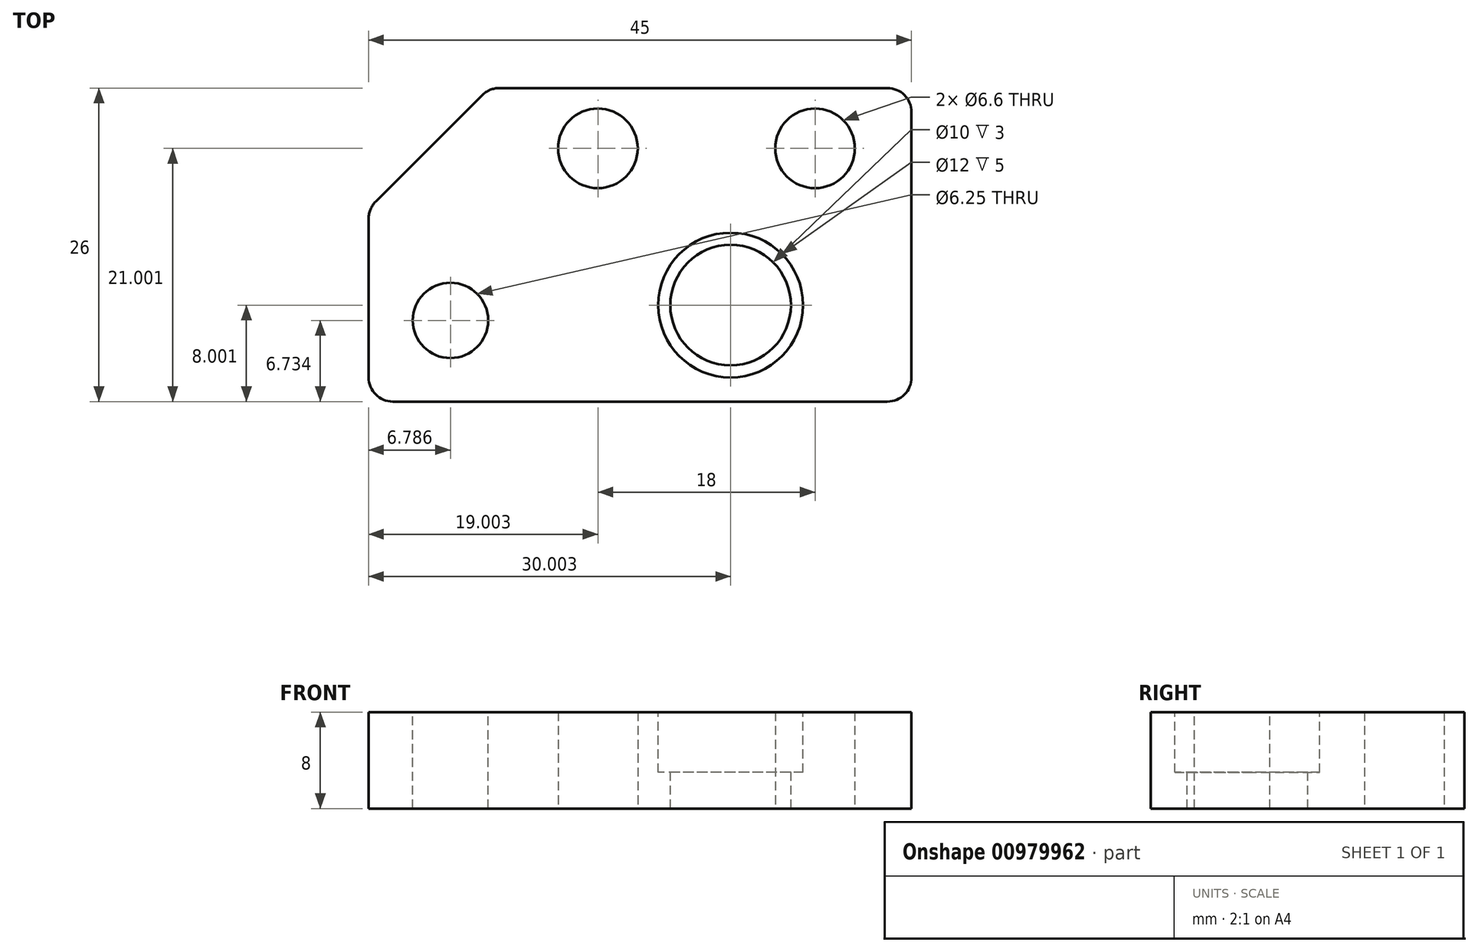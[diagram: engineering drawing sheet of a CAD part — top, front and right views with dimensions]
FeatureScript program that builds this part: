
annotation { "Feature Type Name" : "Feature", "Feature Type Description" : "" }
export const myFeature = defineFeature(function(context is Context, id is Id, definition is map)
    precondition{}
    {
        {
            var Q0;
            Q0=qCreatedBy(makeId("Top.planeOp"),FACE);
            var sketch = newSketch(context, id + "F0", { "sketchPlane" : qUnion([Q0])});
            skLineSegment(sketch, "E0", {"start": v(-26.32, -9.83) * mm, "end": v(14.68, -9.83) * mm});
            skLineSegment(sketch, "E1", {"start": v(16.68, -7.83) * mm, "end": v(16.68, 14.17) * mm});
            skLineSegment(sketch, "E2", {"start": v(14.68, 16.17) * mm, "end": v(-17.49, 16.17) * mm});
            skLineSegment(sketch, "E3", {"start": v(-18.9, 15.59) * mm, "end": v(-27.73, 6.76) * mm});
            skLineSegment(sketch, "E4", {"start": v(-28.32, 5.34) * mm, "end": v(-28.32, -7.83) * mm});
            skPoint(sketch, "E5.visualSharp", {"position": v(-28.32, 6.17) * mm});
            skArc(sketch, "E5.filletArc", {"start": v(-27.73, 6.76) * mm, "mid": v(-28.16, 6.1) * mm, "end": v(-28.32, 5.34) * mm});
            skPoint(sketch, "E6.visualSharp", {"position": v(16.68, 16.17) * mm});
            skArc(sketch, "E6.filletArc", {"start": v(16.68, 14.17) * mm, "mid": v(16.1, 15.59) * mm, "end": v(14.68, 16.17) * mm});
            skPoint(sketch, "E7.visualSharp", {"position": v(-18.32, 16.17) * mm});
            skArc(sketch, "E7.filletArc", {"start": v(-17.49, 16.17) * mm, "mid": v(-18.25, 16.02) * mm, "end": v(-18.9, 15.59) * mm});
            skPoint(sketch, "E8.visualSharp", {"position": v(16.68, -9.83) * mm});
            skArc(sketch, "E8.filletArc", {"start": v(14.68, -9.83) * mm, "mid": v(16.1, -9.24) * mm, "end": v(16.68, -7.83) * mm});
            skPoint(sketch, "E9.visualSharp", {"position": v(-28.32, -9.83) * mm});
            skArc(sketch, "E9.filletArc", {"start": v(-28.32, -7.83) * mm, "mid": v(-27.73, -9.24) * mm, "end": v(-26.32, -9.83) * mm});
            skSolve(sketch);
        }
        {
            var Q0;
            Q0 = qSketchRegion(id + "F0", true);
            extrude(context, id + "F1", {"entities" : qUnion([Q0]), "depth" : 8 * mm, "offsetDistance" : 25.4 * mm});
        }
        {
            var Q0;
            Q0=makeQuery(id+"F1.opExtrude","CAP_FACE",FACE,{"disambiguationData":[OSD([sQuery(id+"F0.wireOp",EDGE,"E0"),sQuery(id+"F0.wireOp",EDGE,"E1"),sQuery(id+"F0.wireOp",EDGE,"E2"),sQuery(id+"F0.wireOp",EDGE,"E3"),sQuery(id+"F0.wireOp",EDGE,"E4"),sQuery(id+"F0.wireOp",EDGE,"E5.filletArc"),sQuery(id+"F0.wireOp",EDGE,"E6.filletArc"),sQuery(id+"F0.wireOp",EDGE,"E7.filletArc"),sQuery(id+"F0.wireOp",EDGE,"E8.filletArc"),sQuery(id+"F0.wireOp",EDGE,"E9.filletArc")])],"isStart":false});
            var sketch = newSketch(context, id + "F2", { "sketchPlane" : qUnion([Q0])});
            skCircle(sketch, "E10", {"center": v(1.68, -1.83) * mm, "radius": 5 * mm});
            skSolve(sketch);
        }
        {
            var Q0;
            Q0 = qSketchRegion(id + "F2", true);
            extrude(context, id + "F3", {"entities" : qUnion([Q0]), "operationType" : NewBodyOperationType.REMOVE, "endBound" : BoundingType.THROUGH_ALL, "oppositeDirection" : true, "depth" : 25.4 * mm, "offsetDistance" : 25.4 * mm});
        }
        {
            var Q0;
            Q0=makeQuery(id+"F1.opExtrude","CAP_FACE",FACE,{"disambiguationData":[OSD([sQuery(id+"F0.wireOp",EDGE,"E0"),sQuery(id+"F0.wireOp",EDGE,"E1"),sQuery(id+"F0.wireOp",EDGE,"E2"),sQuery(id+"F0.wireOp",EDGE,"E3"),sQuery(id+"F0.wireOp",EDGE,"E4"),sQuery(id+"F0.wireOp",EDGE,"E5.filletArc"),sQuery(id+"F0.wireOp",EDGE,"E6.filletArc"),sQuery(id+"F0.wireOp",EDGE,"E7.filletArc"),sQuery(id+"F0.wireOp",EDGE,"E8.filletArc"),sQuery(id+"F0.wireOp",EDGE,"E9.filletArc")])],"isStart":false});
            var sketch = newSketch(context, id + "F4", { "sketchPlane" : qUnion([Q0])});
            skCircle(sketch, "E11", {"center": v(1.68, -1.83) * mm, "radius": 6 * mm});
            skSolve(sketch);
        }
        {
            var Q0;
            Q0 = qSketchRegion(id + "F4", true);
            extrude(context, id + "F5", {"entities" : qUnion([Q0]), "operationType" : NewBodyOperationType.REMOVE, "oppositeDirection" : true, "depth" : 5 * mm, "offsetDistance" : 25.4 * mm});
        }
        {
            var Q0;
            Q0=makeQuery(id+"F1.opExtrude","CAP_FACE",FACE,{"disambiguationData":[OSD([sQuery(id+"F0.wireOp",EDGE,"E0"),sQuery(id+"F0.wireOp",EDGE,"E1"),sQuery(id+"F0.wireOp",EDGE,"E2"),sQuery(id+"F0.wireOp",EDGE,"E3"),sQuery(id+"F0.wireOp",EDGE,"E4"),sQuery(id+"F0.wireOp",EDGE,"E5.filletArc"),sQuery(id+"F0.wireOp",EDGE,"E6.filletArc"),sQuery(id+"F0.wireOp",EDGE,"E7.filletArc"),sQuery(id+"F0.wireOp",EDGE,"E8.filletArc"),sQuery(id+"F0.wireOp",EDGE,"E9.filletArc")])],"isStart":false});
            var sketch = newSketch(context, id + "F6", { "sketchPlane" : qUnion([Q0])});
            skPoint(sketch, "E12", {"position": v(-9.32, 11.17) * mm});
            skPoint(sketch, "E13", {"position": v(8.68, 11.17) * mm});
            skSolve(sketch);
        }
        {
            var Q0;
            Q0=sQuery(id+"F6.wireOp",VERTEX,"E12");
            var Q1;
            Q1=sQuery(id+"F6.wireOp",VERTEX,"E13");
            var Q2;
            Q2=makeQuery(id+"F1.opExtrude","SWEPT_BODY",BODY,{"disambiguationData":[OSD([sQuery(id+"F0.wireOp",EDGE,"E0"),sQuery(id+"F0.wireOp",EDGE,"E1"),sQuery(id+"F0.wireOp",EDGE,"E2"),sQuery(id+"F0.wireOp",EDGE,"E3"),sQuery(id+"F0.wireOp",EDGE,"E4"),sQuery(id+"F0.wireOp",EDGE,"E5.filletArc"),sQuery(id+"F0.wireOp",EDGE,"E6.filletArc"),sQuery(id+"F0.wireOp",EDGE,"E7.filletArc"),sQuery(id+"F0.wireOp",EDGE,"E8.filletArc"),sQuery(id+"F0.wireOp",EDGE,"E9.filletArc")])]});
            hole(context, id + "F7", {"style" : HoleStyle.SIMPLE, "endStyle" : HoleEndStyle.THROUGH, "standardTappedOrClearance" : lookupTablePath({ "fit" : "Normal", "standard" : "ISO", "size" : "M6", "type" : "Clearance" }), "standardBlindInLast" : lookupTablePath({ "fit" : "Normal", "standard" : "ISO", "engagement" : "75%", "pitch" : "1 mm", "size" : "M6", "type" : "Clearance & tapped" }), "holeDiameter" : 6.6 * mm, "majorDiameter" : 6.35 * mm, "isTappedThrough" : true, "tappedDepth" : 12.7 * mm, "tapClearance" : 3, "locations" : qUnion([Q0, Q1]), "scope" : qUnion([Q2]), "startStyle" : HoleStartStyle.PART});
        }
        {
            var Q0;
            Q0=makeQuery(id+"F1.opExtrude","CAP_FACE",FACE,{"disambiguationData":[OSD([sQuery(id+"F0.wireOp",EDGE,"E0"),sQuery(id+"F0.wireOp",EDGE,"E1"),sQuery(id+"F0.wireOp",EDGE,"E2"),sQuery(id+"F0.wireOp",EDGE,"E3"),sQuery(id+"F0.wireOp",EDGE,"E4"),sQuery(id+"F0.wireOp",EDGE,"E5.filletArc"),sQuery(id+"F0.wireOp",EDGE,"E6.filletArc"),sQuery(id+"F0.wireOp",EDGE,"E7.filletArc"),sQuery(id+"F0.wireOp",EDGE,"E8.filletArc"),sQuery(id+"F0.wireOp",EDGE,"E9.filletArc")])],"isStart":false});
            var sketch = newSketch(context, id + "F8", { "sketchPlane" : qUnion([Q0])});
            skCircle(sketch, "E14", {"center": v(-21.53, -3.1) * mm, "radius": 3.12 * mm});
            skSolve(sketch);
        }
        {
            var Q0;
            Q0 = qSketchRegion(id + "F8", true);
            extrude(context, id + "F9", {"entities" : qUnion([Q0]), "operationType" : NewBodyOperationType.REMOVE, "endBound" : BoundingType.THROUGH_ALL, "oppositeDirection" : true, "depth" : 4 * mm, "offsetDistance" : 25.4 * mm});
        }
    });
